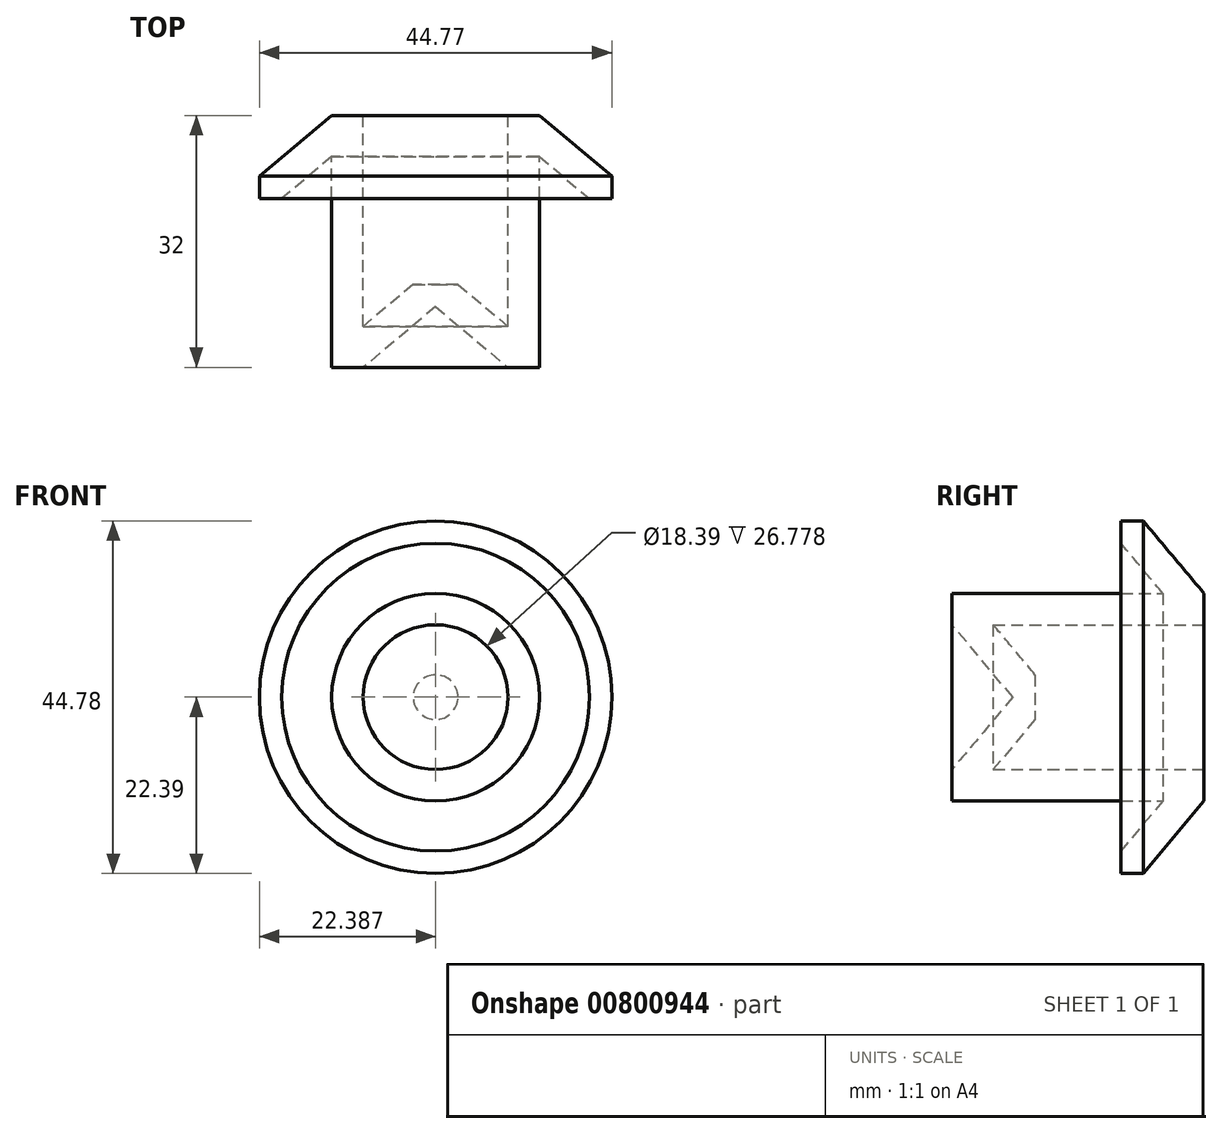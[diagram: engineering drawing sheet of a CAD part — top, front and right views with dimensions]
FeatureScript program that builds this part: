
annotation { "Feature Type Name" : "Feature", "Feature Type Description" : "" }
export const myFeature = defineFeature(function(context is Context, id is Id, definition is map)
    precondition{}
    {
        {
            var Q0;
            Q0=qCreatedBy(makeId("Top.planeOp"),FACE);
            var sketch = newSketch(context, id + "F0", { "sketchPlane" : qUnion([Q0])});
            skLineSegment(sketch, "E0", {"start": v(0, 0) * mm, "end": v(0, -26.78) * mm});
            skLineSegment(sketch, "E1", {"start": v(0, -26.78) * mm, "end": v(-6.35, -21.45) * mm});
            skLineSegment(sketch, "E2", {"start": v(-6.35, -21.45) * mm, "end": v(-9.2, -21.45) * mm});
            skLineSegment(sketch, "E3", {"start": v(-9.2, -21.45) * mm, "end": v(-9.2, -24.29) * mm});
            skLineSegment(sketch, "E4", {"start": v(-9.2, -24.29) * mm, "end": v(0, -32) * mm});
            skLineSegment(sketch, "E5", {"start": v(0, -32) * mm, "end": v(4, -32) * mm});
            skLineSegment(sketch, "E6", {"start": v(4, -32) * mm, "end": v(4, -5.22) * mm});
            skLineSegment(sketch, "E7", {"start": v(4, -5.22) * mm, "end": v(10.35, -10.55) * mm});
            skLineSegment(sketch, "E8", {"start": v(10.35, -10.55) * mm, "end": v(13.2, -10.55) * mm});
            skLineSegment(sketch, "E9", {"start": v(13.2, -10.55) * mm, "end": v(13.2, -7.71) * mm});
            skLineSegment(sketch, "E10", {"start": v(13.2, -7.71) * mm, "end": v(4, 0) * mm});
            skLineSegment(sketch, "E11", {"start": v(4, 0) * mm, "end": v(0, 0) * mm});
            skSolve(sketch);
        }
        {
            var Q0;
            Q0=makeQuery(id+"F0.imprint","IMPRINT",FACE,{"disambiguationData":[TD([[makeQuery(id+"F0.imprint","IMPRINT",EDGE,{"derivedFrom":sQuery(id+"F0.wireOp",EDGE,"E0")}),1.0]])]});
            var Q1;
            Q1=sQuery(id+"F0.wireOp",EDGE,"E3");
            revolve(context, id + "F1", {"surfaceOperationType" : NewSurfaceOperationType.NEW, "entities" : qUnion([Q0]), "axis" : qUnion([Q1]), "revolveType" : RevolveType.FULL});
        }
    });
